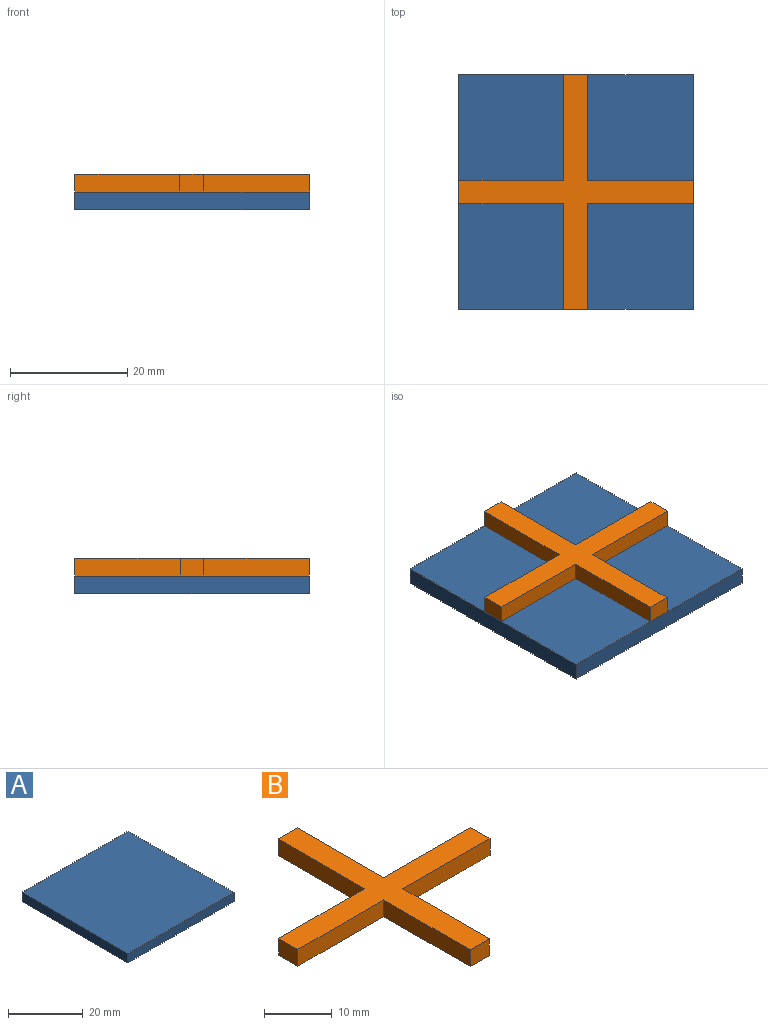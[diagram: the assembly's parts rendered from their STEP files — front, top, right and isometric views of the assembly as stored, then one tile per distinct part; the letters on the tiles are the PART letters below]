
ASSEMBLY  parts=2 mates=1
PART A: 6 faces, bbox 40x40x3 mm
  f0: plane 40x3mm, normal (0,1,0), area 120mm2, adj f1,f3,f4,f5
  f1: plane 40x3mm, normal (-1,0,0), area 120mm2, adj f0,f2,f4,f5
  f2: plane 40x3mm, normal (0,-1,0), area 120mm2, adj f1,f3,f4,f5
  f3: plane 40x3mm, normal (1,0,0), area 120mm2, adj f0,f2,f4,f5
  f4: plane 40x40mm, normal (0,0,1), area 1600mm2, adj f0,f1,f2,f3
  f5: plane 40x40mm, normal (0,0,-1), area 1600mm2, adj f0,f1,f2,f3
PART B: 14 faces, bbox 40x40x3 mm
  f0: plane 4x3mm, normal (-1,0,0), area 12mm2, adj f1,f11,f12,f13
  f1: plane 17.89x3mm, normal (0,-1,0), area 53.7mm2, adj f0,f2,f12,f13
  f2: plane 18x3mm, normal (-1,0,0), area 54mm2, adj f1,f3,f12,f13
  f3: plane 4x3mm, normal (0,-1,0), area 12mm2, adj f2,f4,f12,f13
  f4: plane 18x3mm, normal (1,0,0), area 54mm2, adj f3,f5,f12,f13
  f5: plane 18.12x3mm, normal (0,-1,0), area 54.3mm2, adj f4,f6,f12,f13
  f6: plane 4x3mm, normal (1,0,0), area 12mm2, adj f5,f7,f12,f13
  f7: plane 18.12x3mm, normal (0,1,0), area 54.3mm2, adj f6,f8,f12,f13
  f8: plane 18x3mm, normal (1,0,0), area 54mm2, adj f7,f9,f12,f13
  f9: plane 4x3mm, normal (0,1,0), area 12mm2, adj f8,f10,f12,f13
  f10: plane 18x3mm, normal (-1,0,0), area 54mm2, adj f9,f11,f12,f13
  f11: plane 17.89x3mm, normal (0,1,0), area 53.7mm2, adj f0,f10,f12,f13
  f12: plane 40x40mm, normal (0,0,1), area 304mm2, adj f0,f1,f2,f3,f4,f5,f6,f7
  f13: plane 40x40mm, normal (0,0,-1), area 304mm2, adj f0,f1,f2,f3,f4,f5,f6,f7
PLACE A t=(36.63,-3.53,13.22)mm
PLACE B t=(37.57,-1.96,16.22)mm
MATE slider A.f4 <-> B.f13  axis (0,0,1) through (37.63,-1.96,16.22)mm
